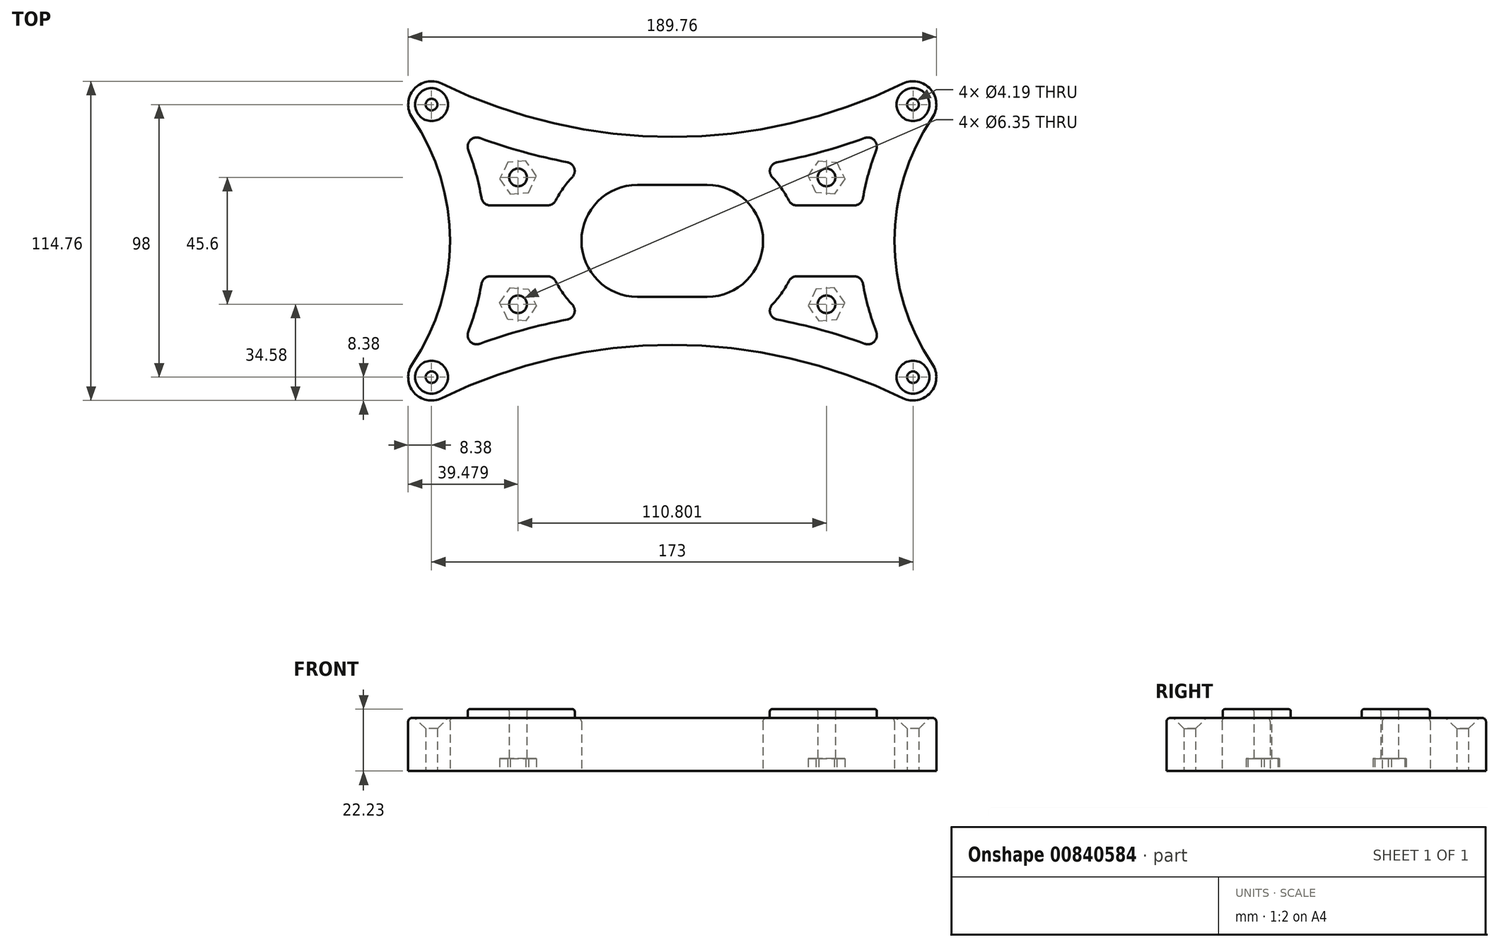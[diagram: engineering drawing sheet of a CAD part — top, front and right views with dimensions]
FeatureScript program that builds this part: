
annotation { "Feature Type Name" : "Feature", "Feature Type Description" : "" }
export const myFeature = defineFeature(function(context is Context, id is Id, definition is map)
    precondition{}
    {
        {
            var Q0;
            Q0=qCreatedBy(makeId("Top.planeOp"),FACE);
            var sketch = newSketch(context, id + "F0", { "sketchPlane" : qUnion([Q0])});
            skLineSegment(sketch, "E0.bottom", {"start": v(-102.5, 65) * mm, "end": v(102.5, 65) * mm, "construction": true});
            skLineSegment(sketch, "E0.top", {"start": v(-102.5, -65) * mm, "end": v(102.5, -65) * mm, "construction": true});
            skLineSegment(sketch, "E0.left", {"start": v(-102.5, 65) * mm, "end": v(-102.5, -65) * mm, "construction": true});
            skLineSegment(sketch, "E0.right", {"start": v(102.5, 65) * mm, "end": v(102.5, -65) * mm, "construction": true});
            skPoint(sketch, "E0.middle", {"position": v(0, 0) * mm});
            skArc(sketch, "E1", {"start": v(-79.48, 63.38) * mm, "mid": v(-98.58, 59.5) * mm, "end": v(-99.76, 40.04) * mm, "construction": true});
            skArc(sketch, "E2.MirrorC", {"start": v(79.48, 63.38) * mm, "mid": v(98.58, 59.5) * mm, "end": v(99.76, 40.04) * mm, "construction": true});
            skArc(sketch, "E3.MirrorC", {"start": v(79.48, -63.38) * mm, "mid": v(98.58, -59.5) * mm, "end": v(99.76, -40.04) * mm, "construction": true});
            skArc(sketch, "E4.MirrorC", {"start": v(-79.48, -63.38) * mm, "mid": v(-98.58, -59.5) * mm, "end": v(-99.76, -40.04) * mm, "construction": true});
            skLineSegment(sketch, "E5", {"start": v(0, 0) * mm, "end": v(0, 365.73) * mm, "construction": true});
            skPoint(sketch, "E5.endSnap0", {"position": v(0, 65) * mm});
            skLineSegment(sketch, "E6", {"start": v(0, 0) * mm, "end": v(0, -420.15) * mm, "construction": true});
            skLineSegment(sketch, "E7", {"start": v(0, 0) * mm, "end": v(397.25, 0) * mm, "construction": true});
            skPoint(sketch, "E7.endSnap0", {"position": v(102.5, 0) * mm});
            skLineSegment(sketch, "E8", {"start": v(0, 0) * mm, "end": v(-430.2, 0) * mm, "construction": true});
            skPoint(sketch, "E9", {"position": v(0, 45) * mm});
            skPoint(sketch, "E10", {"position": v(0, -45) * mm});
            skPoint(sketch, "E11", {"position": v(-87.5, 0) * mm});
            skPoint(sketch, "E12", {"position": v(87.5, 0) * mm});
            skArc(sketch, "E13", {"start": v(-79.48, 63.38) * mm, "mid": v(0, 45) * mm, "end": v(79.48, 63.38) * mm, "construction": true});
            skArc(sketch, "E14.MirrorC", {"start": v(-79.48, -63.38) * mm, "mid": v(0, -45) * mm, "end": v(79.48, -63.38) * mm, "construction": true});
            skArc(sketch, "E15", {"start": v(99.76, 40.04) * mm, "mid": v(87.5, 0) * mm, "end": v(99.76, -40.04) * mm, "construction": true});
            skArc(sketch, "E16.MirrorC", {"start": v(-99.76, 40.04) * mm, "mid": v(-87.5, 0) * mm, "end": v(-99.76, -40.04) * mm, "construction": true});
            skArc(sketch, "E17", {"start": v(-12.5, 12.5) * mm, "mid": v(-25, 0) * mm, "end": v(-12.5, -12.5) * mm, "construction": true});
            skArc(sketch, "E18.MirrorC", {"start": v(12.5, 12.5) * mm, "mid": v(25, 0) * mm, "end": v(12.5, -12.5) * mm, "construction": true});
            skLineSegment(sketch, "E19", {"start": v(-12.5, 12.5) * mm, "end": v(12.5, 12.5) * mm, "construction": true});
            skLineSegment(sketch, "E20", {"start": v(-12.5, -12.5) * mm, "end": v(12.5, -12.5) * mm, "construction": true});
            skArc(sketch, "E21.0", {"start": v(73.54, 32.7) * mm, "mid": v(70.75, 24.17) * mm, "end": v(68.8, 15.41) * mm, "construction": true});
            skArc(sketch, "E21.1", {"start": v(-69.07, 37.24) * mm, "mid": v(-53.53, 32.26) * mm, "end": v(-37.64, 28.55) * mm, "construction": true});
            skArc(sketch, "E21.2", {"start": v(-73.54, 32.7) * mm, "mid": v(-70.75, 24.17) * mm, "end": v(-68.8, 15.41) * mm, "construction": true});
            skArc(sketch, "E21.3", {"start": v(-69.07, -37.24) * mm, "mid": v(-53.53, -32.26) * mm, "end": v(-37.64, -28.55) * mm, "construction": true});
            skArc(sketch, "E22.0", {"start": v(-35.78, 22.67) * mm, "mid": v(-39.02, 18.79) * mm, "end": v(-41.61, 14.44) * mm, "construction": true});
            skArc(sketch, "E22.2", {"start": v(35.78, 22.67) * mm, "mid": v(39.02, 18.79) * mm, "end": v(41.61, 14.44) * mm, "construction": true});
            skPoint(sketch, "E23.visualSharp", {"position": v(-76.83, 40.26) * mm});
            skArc(sketch, "E23.filletArc", {"start": v(-69.07, 37.24) * mm, "mid": v(-72.76, 36.4) * mm, "end": v(-73.54, 32.7) * mm, "construction": true});
            skLineSegment(sketch, "E24", {"start": v(-44.75, 12.5) * mm, "end": v(-65.36, 12.5) * mm, "construction": true});
            skLineSegment(sketch, "E25", {"start": v(-44.75, -12.5) * mm, "end": v(-65.36, -12.5) * mm, "construction": true});
            skLineSegment(sketch, "E26", {"start": v(44.75, 12.5) * mm, "end": v(65.36, 12.5) * mm, "construction": true});
            skLineSegment(sketch, "E27", {"start": v(44.75, -12.5) * mm, "end": v(65.36, -12.5) * mm, "construction": true});
            skArc(sketch, "E28.trimOffspring", {"start": v(41.61, -14.44) * mm, "mid": v(39.02, -18.79) * mm, "end": v(35.78, -22.67) * mm, "construction": true});
            skArc(sketch, "E29.trimOffspring", {"start": v(68.8, -15.41) * mm, "mid": v(70.75, -24.17) * mm, "end": v(73.54, -32.7) * mm, "construction": true});
            skArc(sketch, "E30.trimOffspring", {"start": v(37.64, 28.55) * mm, "mid": v(53.53, 32.26) * mm, "end": v(69.07, 37.24) * mm, "construction": true});
            skArc(sketch, "E31.trimOffspring", {"start": v(37.64, -28.55) * mm, "mid": v(53.53, -32.26) * mm, "end": v(69.07, -37.24) * mm, "construction": true});
            skArc(sketch, "E32.trimOffspring", {"start": v(-41.61, -14.44) * mm, "mid": v(-39.02, -18.79) * mm, "end": v(-35.78, -22.67) * mm, "construction": true});
            skArc(sketch, "E33.trimOffspring", {"start": v(-68.8, -15.41) * mm, "mid": v(-70.75, -24.17) * mm, "end": v(-73.54, -32.7) * mm, "construction": true});
            skPoint(sketch, "E34.visualSharp", {"position": v(-30.17, 27.28) * mm});
            skArc(sketch, "E34.filletArc", {"start": v(-35.78, 22.67) * mm, "mid": v(-34.95, 26.17) * mm, "end": v(-37.64, 28.55) * mm, "construction": true});
            skPoint(sketch, "E35.visualSharp", {"position": v(-42.5, 12.5) * mm});
            skArc(sketch, "E35.filletArc", {"start": v(-44.75, 12.5) * mm, "mid": v(-42.9, 13.03) * mm, "end": v(-41.61, 14.44) * mm, "construction": true});
            skPoint(sketch, "E36.visualSharp", {"position": v(-68.36, 12.5) * mm});
            skArc(sketch, "E36.filletArc", {"start": v(-68.8, 15.41) * mm, "mid": v(-67.61, 13.32) * mm, "end": v(-65.36, 12.5) * mm, "construction": true});
            skPoint(sketch, "E37.visualSharp", {"position": v(-68.36, -12.5) * mm});
            skArc(sketch, "E37.filletArc", {"start": v(-65.36, -12.5) * mm, "mid": v(-67.61, -13.32) * mm, "end": v(-68.8, -15.41) * mm, "construction": true});
            skPoint(sketch, "E38.visualSharp", {"position": v(-42.5, -12.5) * mm});
            skArc(sketch, "E38.filletArc", {"start": v(-41.61, -14.44) * mm, "mid": v(-42.9, -13.03) * mm, "end": v(-44.75, -12.5) * mm, "construction": true});
            skPoint(sketch, "E39.visualSharp", {"position": v(-30.17, -27.28) * mm});
            skArc(sketch, "E39.filletArc", {"start": v(-37.64, -28.55) * mm, "mid": v(-34.95, -26.17) * mm, "end": v(-35.78, -22.67) * mm, "construction": true});
            skPoint(sketch, "E40.visualSharp", {"position": v(-76.83, -40.26) * mm});
            skArc(sketch, "E40.filletArc", {"start": v(-73.54, -32.7) * mm, "mid": v(-72.76, -36.4) * mm, "end": v(-69.07, -37.24) * mm, "construction": true});
            skPoint(sketch, "E41.visualSharp", {"position": v(30.17, 27.28) * mm});
            skArc(sketch, "E41.filletArc", {"start": v(37.64, 28.55) * mm, "mid": v(34.95, 26.17) * mm, "end": v(35.78, 22.67) * mm, "construction": true});
            skPoint(sketch, "E42.visualSharp", {"position": v(76.83, 40.26) * mm});
            skArc(sketch, "E42.filletArc", {"start": v(73.54, 32.7) * mm, "mid": v(72.76, 36.4) * mm, "end": v(69.07, 37.24) * mm, "construction": true});
            skPoint(sketch, "E43.visualSharp", {"position": v(68.36, 12.5) * mm});
            skArc(sketch, "E43.filletArc", {"start": v(65.36, 12.5) * mm, "mid": v(67.61, 13.32) * mm, "end": v(68.8, 15.41) * mm, "construction": true});
            skPoint(sketch, "E44.visualSharp", {"position": v(42.5, 12.5) * mm});
            skArc(sketch, "E44.filletArc", {"start": v(41.61, 14.44) * mm, "mid": v(42.9, 13.03) * mm, "end": v(44.75, 12.5) * mm, "construction": true});
            skPoint(sketch, "E45.visualSharp", {"position": v(42.5, -12.5) * mm});
            skArc(sketch, "E45.filletArc", {"start": v(44.75, -12.5) * mm, "mid": v(42.9, -13.03) * mm, "end": v(41.61, -14.44) * mm, "construction": true});
            skPoint(sketch, "E46.visualSharp", {"position": v(68.36, -12.5) * mm});
            skArc(sketch, "E46.filletArc", {"start": v(68.8, -15.41) * mm, "mid": v(67.61, -13.32) * mm, "end": v(65.36, -12.5) * mm, "construction": true});
            skPoint(sketch, "E47.visualSharp", {"position": v(76.83, -40.26) * mm});
            skArc(sketch, "E47.filletArc", {"start": v(69.07, -37.24) * mm, "mid": v(72.76, -36.4) * mm, "end": v(73.54, -32.7) * mm, "construction": true});
            skPoint(sketch, "E48.visualSharp", {"position": v(30.17, -27.28) * mm});
            skArc(sketch, "E48.filletArc", {"start": v(35.78, -22.67) * mm, "mid": v(34.95, -26.17) * mm, "end": v(37.64, -28.55) * mm, "construction": true});
            skArc(sketch, "E49.0", {"start": v(-82.82, 56.53) * mm, "mid": v(-92.82, 54.5) * mm, "end": v(-93.44, 44.3) * mm});
            skArc(sketch, "E49.1", {"start": v(-93.44, 44.3) * mm, "mid": v(-79.88, 0) * mm, "end": v(-93.44, -44.3) * mm});
            skArc(sketch, "E49.2", {"start": v(-82.82, 56.53) * mm, "mid": v(0, 37.38) * mm, "end": v(82.82, 56.53) * mm});
            skArc(sketch, "E49.3", {"start": v(-82.82, -56.53) * mm, "mid": v(-92.82, -54.5) * mm, "end": v(-93.44, -44.3) * mm});
            skArc(sketch, "E49.4", {"start": v(82.82, 56.53) * mm, "mid": v(92.82, 54.5) * mm, "end": v(93.44, 44.3) * mm});
            skArc(sketch, "E49.5", {"start": v(93.44, 44.3) * mm, "mid": v(79.88, 0) * mm, "end": v(93.44, -44.3) * mm});
            skArc(sketch, "E49.6", {"start": v(82.82, -56.53) * mm, "mid": v(92.82, -54.5) * mm, "end": v(93.44, -44.3) * mm});
            skArc(sketch, "E49.7", {"start": v(-82.82, -56.53) * mm, "mid": v(0, -37.38) * mm, "end": v(82.82, -56.53) * mm});
            skCircle(sketch, "E50", {"center": v(-86.5, -49) * mm, "radius": 2.1 * mm});
            skCircle(sketch, "E51", {"center": v(86.5, -49) * mm, "radius": 2.1 * mm});
            skCircle(sketch, "E52", {"center": v(86.5, 49) * mm, "radius": 2.1 * mm});
            skCircle(sketch, "E53", {"center": v(-86.5, 49) * mm, "radius": 2.1 * mm});
            skArc(sketch, "E54.0", {"start": v(-41.84, -14.56) * mm, "mid": v(-43.04, -13.24) * mm, "end": v(-44.75, -12.75) * mm});
            skArc(sketch, "E54.1", {"start": v(-41.84, -14.56) * mm, "mid": v(-39.23, -18.93) * mm, "end": v(-35.97, -22.85) * mm});
            skLineSegment(sketch, "E54.2", {"start": v(-44.75, -12.75) * mm, "end": v(-65.36, -12.75) * mm});
            skArc(sketch, "E54.3", {"start": v(-37.68, -28.3) * mm, "mid": v(-35.2, -26.1) * mm, "end": v(-35.97, -22.85) * mm});
            skArc(sketch, "E54.4", {"start": v(-65.36, -12.75) * mm, "mid": v(-67.45, -13.52) * mm, "end": v(-68.56, -15.45) * mm});
            skArc(sketch, "E54.5", {"start": v(-68.56, -15.45) * mm, "mid": v(-70.5, -24.24) * mm, "end": v(-73.3, -32.79) * mm});
            skArc(sketch, "E54.6", {"start": v(-73.3, -32.79) * mm, "mid": v(-72.58, -36.23) * mm, "end": v(-69.16, -37) * mm});
            skArc(sketch, "E54.7", {"start": v(-69.16, -37) * mm, "mid": v(-53.6, -32.01) * mm, "end": v(-37.68, -28.3) * mm});
            skArc(sketch, "E55.0", {"start": v(68.56, -15.45) * mm, "mid": v(67.45, -13.52) * mm, "end": v(65.36, -12.75) * mm});
            skLineSegment(sketch, "E55.1", {"start": v(44.75, -12.75) * mm, "end": v(65.36, -12.75) * mm});
            skArc(sketch, "E55.2", {"start": v(68.56, -15.45) * mm, "mid": v(70.5, -24.24) * mm, "end": v(73.3, -32.79) * mm});
            skArc(sketch, "E55.3", {"start": v(44.75, -12.75) * mm, "mid": v(43.04, -13.24) * mm, "end": v(41.84, -14.56) * mm});
            skArc(sketch, "E55.4", {"start": v(69.16, -37) * mm, "mid": v(72.58, -36.23) * mm, "end": v(73.3, -32.79) * mm});
            skArc(sketch, "E55.5", {"start": v(37.68, -28.3) * mm, "mid": v(53.6, -32.01) * mm, "end": v(69.16, -37) * mm});
            skArc(sketch, "E55.6", {"start": v(35.97, -22.85) * mm, "mid": v(35.2, -26.1) * mm, "end": v(37.68, -28.3) * mm});
            skArc(sketch, "E55.7", {"start": v(41.84, -14.56) * mm, "mid": v(39.23, -18.93) * mm, "end": v(35.97, -22.85) * mm});
            skArc(sketch, "E56.0", {"start": v(37.68, 28.3) * mm, "mid": v(35.2, 26.1) * mm, "end": v(35.97, 22.85) * mm});
            skArc(sketch, "E56.1", {"start": v(35.97, 22.85) * mm, "mid": v(39.23, 18.93) * mm, "end": v(41.84, 14.56) * mm});
            skArc(sketch, "E56.2", {"start": v(37.68, 28.3) * mm, "mid": v(53.6, 32.01) * mm, "end": v(69.16, 37) * mm});
            skArc(sketch, "E56.3", {"start": v(41.84, 14.56) * mm, "mid": v(43.04, 13.24) * mm, "end": v(44.75, 12.75) * mm});
            skArc(sketch, "E56.4", {"start": v(73.3, 32.79) * mm, "mid": v(72.58, 36.23) * mm, "end": v(69.16, 37) * mm});
            skArc(sketch, "E56.5", {"start": v(73.3, 32.79) * mm, "mid": v(70.5, 24.24) * mm, "end": v(68.56, 15.45) * mm});
            skArc(sketch, "E56.6", {"start": v(65.36, 12.75) * mm, "mid": v(67.45, 13.52) * mm, "end": v(68.56, 15.45) * mm});
            skLineSegment(sketch, "E56.7", {"start": v(44.75, 12.75) * mm, "end": v(65.36, 12.75) * mm});
            skArc(sketch, "E57.0", {"start": v(-69.16, 37) * mm, "mid": v(-72.58, 36.23) * mm, "end": v(-73.3, 32.79) * mm});
            skArc(sketch, "E57.1", {"start": v(-73.3, 32.79) * mm, "mid": v(-70.5, 24.24) * mm, "end": v(-68.56, 15.45) * mm});
            skArc(sketch, "E57.2", {"start": v(-69.16, 37) * mm, "mid": v(-53.6, 32.01) * mm, "end": v(-37.68, 28.3) * mm});
            skArc(sketch, "E57.3", {"start": v(-68.56, 15.45) * mm, "mid": v(-67.45, 13.52) * mm, "end": v(-65.36, 12.75) * mm});
            skArc(sketch, "E57.4", {"start": v(-35.97, 22.85) * mm, "mid": v(-35.2, 26.1) * mm, "end": v(-37.68, 28.3) * mm});
            skArc(sketch, "E57.5", {"start": v(-35.97, 22.85) * mm, "mid": v(-39.23, 18.93) * mm, "end": v(-41.84, 14.56) * mm});
            skArc(sketch, "E57.6", {"start": v(-44.75, 12.75) * mm, "mid": v(-43.04, 13.24) * mm, "end": v(-41.84, 14.56) * mm});
            skLineSegment(sketch, "E57.7", {"start": v(-44.75, 12.75) * mm, "end": v(-65.36, 12.75) * mm});
            skLineSegment(sketch, "E58.0", {"start": v(-12.5, 20.12) * mm, "end": v(12.5, 20.12) * mm});
            skArc(sketch, "E58.1", {"start": v(-12.5, 20.12) * mm, "mid": v(-32.62, 0) * mm, "end": v(-12.5, -20.12) * mm});
            skLineSegment(sketch, "E58.2", {"start": v(-12.5, -20.12) * mm, "end": v(12.5, -20.12) * mm});
            skArc(sketch, "E58.3", {"start": v(12.5, 20.12) * mm, "mid": v(32.62, 0) * mm, "end": v(12.5, -20.12) * mm});
            skPoint(sketch, "E59", {"position": v(-55.4, 22.8) * mm});
            skPoint(sketch, "E60.MirrorP", {"position": v(-55.4, -22.8) * mm});
            skPoint(sketch, "E61.MirrorP", {"position": v(55.4, -22.8) * mm});
            skPoint(sketch, "E62.MirrorP", {"position": v(55.4, 22.8) * mm});
            skCircle(sketch, "E63", {"center": v(-55.4, -22.8) * mm, "radius": 3.18 * mm});
            skCircle(sketch, "E64.cCircle", {"center": v(-55.4, -22.8) * mm, "radius": 5.72 * mm, "construction": true});
            skLineSegment(sketch, "E64.0", {"start": v(-61.98, -22.26) * mm, "end": v(-58.22, -16.83) * mm});
            skLineSegment(sketch, "E64.1", {"start": v(-58.22, -16.83) * mm, "end": v(-51.64, -17.37) * mm});
            skLineSegment(sketch, "E64.2", {"start": v(-51.64, -17.37) * mm, "end": v(-48.82, -23.34) * mm});
            skLineSegment(sketch, "E64.3", {"start": v(-48.82, -23.34) * mm, "end": v(-52.58, -28.77) * mm});
            skLineSegment(sketch, "E64.4", {"start": v(-52.58, -28.77) * mm, "end": v(-59.16, -28.23) * mm});
            skLineSegment(sketch, "E64.5", {"start": v(-59.16, -28.23) * mm, "end": v(-61.98, -22.26) * mm});
            skPoint(sketch, "E64.0.midPoint", {"position": v(-60.1, -19.55) * mm});
            skLineSegment(sketch, "E65.MirrorCS", {"start": v(-51.64, 17.37) * mm, "end": v(-48.82, 23.34) * mm});
            skLineSegment(sketch, "E66.MirrorCS", {"start": v(-61.98, 22.26) * mm, "end": v(-58.22, 16.83) * mm});
            skLineSegment(sketch, "E67.MirrorCS", {"start": v(-52.58, 28.77) * mm, "end": v(-59.16, 28.23) * mm});
            skLineSegment(sketch, "E68.MirrorCS", {"start": v(-59.16, 28.23) * mm, "end": v(-61.98, 22.26) * mm});
            skCircle(sketch, "E69.MirrorC", {"center": v(-55.4, 22.8) * mm, "radius": 3.18 * mm});
            skPoint(sketch, "E70.MirrorP", {"position": v(-60.1, 19.55) * mm});
            skLineSegment(sketch, "E71.MirrorCS", {"start": v(-48.82, 23.34) * mm, "end": v(-52.58, 28.77) * mm});
            skLineSegment(sketch, "E72.MirrorCS", {"start": v(-58.22, 16.83) * mm, "end": v(-51.64, 17.37) * mm});
            skCircle(sketch, "E73.MirrorC", {"center": v(-55.4, 22.8) * mm, "radius": 5.72 * mm, "construction": true});
            skLineSegment(sketch, "E74.MirrorCS", {"start": v(58.22, 16.83) * mm, "end": v(51.64, 17.37) * mm});
            skLineSegment(sketch, "E75.MirrorCS", {"start": v(48.82, 23.34) * mm, "end": v(52.58, 28.77) * mm});
            skPoint(sketch, "E76.MirrorP", {"position": v(60.1, 19.55) * mm});
            skLineSegment(sketch, "E77.MirrorCS", {"start": v(52.58, 28.77) * mm, "end": v(59.16, 28.23) * mm});
            skLineSegment(sketch, "E78.MirrorCS", {"start": v(59.16, 28.23) * mm, "end": v(61.98, 22.26) * mm});
            skCircle(sketch, "E79.MirrorC", {"center": v(55.4, 22.8) * mm, "radius": 5.72 * mm, "construction": true});
            skLineSegment(sketch, "E80.MirrorCS", {"start": v(61.98, 22.26) * mm, "end": v(58.22, 16.83) * mm});
            skLineSegment(sketch, "E81.MirrorCS", {"start": v(51.64, 17.37) * mm, "end": v(48.82, 23.34) * mm});
            skCircle(sketch, "E82.MirrorC", {"center": v(55.4, 22.8) * mm, "radius": 3.18 * mm});
            skLineSegment(sketch, "E83.MirrorCS", {"start": v(48.82, -23.34) * mm, "end": v(52.58, -28.77) * mm});
            skLineSegment(sketch, "E84.MirrorCS", {"start": v(51.64, -17.37) * mm, "end": v(48.82, -23.34) * mm});
            skPoint(sketch, "E85.MirrorP", {"position": v(60.1, -19.55) * mm});
            skLineSegment(sketch, "E86.MirrorCS", {"start": v(59.16, -28.23) * mm, "end": v(61.98, -22.26) * mm});
            skCircle(sketch, "E87.MirrorC", {"center": v(55.4, -22.8) * mm, "radius": 5.72 * mm, "construction": true});
            skLineSegment(sketch, "E88.MirrorCS", {"start": v(61.98, -22.26) * mm, "end": v(58.22, -16.83) * mm});
            skLineSegment(sketch, "E89.MirrorCS", {"start": v(52.58, -28.77) * mm, "end": v(59.16, -28.23) * mm});
            skLineSegment(sketch, "E90.MirrorCS", {"start": v(58.22, -16.83) * mm, "end": v(51.64, -17.37) * mm});
            skCircle(sketch, "E91.MirrorC", {"center": v(55.4, -22.8) * mm, "radius": 3.18 * mm});
            skSolve(sketch);
        }
        {
            var Q0;
            Q0=makeQuery(id+"F0.imprint","IMPRINT",FACE,{"disambiguationData":[TD([[makeQuery(id+"F0.imprint","IMPRINT",EDGE,{"derivedFrom":sQuery(id+"F0.wireOp",EDGE,"E49.0")}),1.0]])]});
            extrude(context, id + "F1", {"entities" : qUnion([Q0]), "depth" : 19.05 * mm, "offsetDistance" : 25.4 * mm});
        }
        {
            var Q0;
            Q0=makeQuery(id+"F0.imprint","IMPRINT",FACE,{"disambiguationData":[TD([[makeQuery(id+"F0.imprint","IMPRINT",EDGE,{"derivedFrom":sQuery(id+"F0.wireOp",EDGE,"E57.0")}),1.0]])]});
            var Q1;
            Q1=makeQuery(id+"F0.imprint","IMPRINT",FACE,{"disambiguationData":[TD([[makeQuery(id+"F0.imprint","IMPRINT",EDGE,{"derivedFrom":sQuery(id+"F0.wireOp",EDGE,"E54.0")}),1.0]])]});
            var Q2;
            Q2=makeQuery(id+"F0.imprint","IMPRINT",FACE,{"disambiguationData":[TD([[makeQuery(id+"F0.imprint","IMPRINT",EDGE,{"derivedFrom":sQuery(id+"F0.wireOp",EDGE,"E55.0")}),1.0]])]});
            var Q3;
            Q3=makeQuery(id+"F0.imprint","IMPRINT",FACE,{"disambiguationData":[TD([[makeQuery(id+"F0.imprint","IMPRINT",EDGE,{"derivedFrom":sQuery(id+"F0.wireOp",EDGE,"E56.0")}),1.0]])]});
            var Q4;
            Q4=makeQuery(id+"F0.imprint","IMPRINT",FACE,{"disambiguationData":[TD([[makeQuery(id+"F0.imprint","IMPRINT",EDGE,{"derivedFrom":sQuery(id+"F0.wireOp",EDGE,"E74.MirrorCS")}),-1.0]])]});
            var Q5;
            Q5=makeQuery(id+"F0.imprint","IMPRINT",FACE,{"disambiguationData":[TD([[makeQuery(id+"F0.imprint","IMPRINT",EDGE,{"derivedFrom":sQuery(id+"F0.wireOp",EDGE,"E83.MirrorCS")}),1.0]])]});
            var Q6;
            Q6=makeQuery(id+"F0.imprint","IMPRINT",FACE,{"disambiguationData":[TD([[makeQuery(id+"F0.imprint","IMPRINT",EDGE,{"derivedFrom":sQuery(id+"F0.wireOp",EDGE,"E63")}),-1.0]])]});
            var Q7;
            Q7=makeQuery(id+"F0.imprint","IMPRINT",FACE,{"disambiguationData":[TD([[makeQuery(id+"F0.imprint","IMPRINT",EDGE,{"derivedFrom":sQuery(id+"F0.wireOp",EDGE,"E65.MirrorCS")}),1.0]])]});
            extrude(context, id + "F2", {"entities" : qUnion([Q0, Q1, Q2, Q3, Q4, Q5, Q6, Q7]), "operationType" : NewBodyOperationType.ADD, "depth" : 22.22 * mm, "offsetDistance" : 25.4 * mm});
        }
        {
            var Q0;
            Q0=makeQuery(id+"F0.imprint","IMPRINT",FACE,{"disambiguationData":[TD([[makeQuery(id+"F0.imprint","IMPRINT",EDGE,{"derivedFrom":sQuery(id+"F0.wireOp",EDGE,"E65.MirrorCS")}),1.0]])]});
            var Q1;
            Q1=makeQuery(id+"F0.imprint","IMPRINT",FACE,{"disambiguationData":[TD([[makeQuery(id+"F0.imprint","IMPRINT",EDGE,{"derivedFrom":sQuery(id+"F0.wireOp",EDGE,"E74.MirrorCS")}),-1.0]])]});
            var Q2;
            Q2=makeQuery(id+"F0.imprint","IMPRINT",FACE,{"disambiguationData":[TD([[makeQuery(id+"F0.imprint","IMPRINT",EDGE,{"derivedFrom":sQuery(id+"F0.wireOp",EDGE,"E83.MirrorCS")}),1.0]])]});
            var Q3;
            Q3=makeQuery(id+"F0.imprint","IMPRINT",FACE,{"disambiguationData":[TD([[makeQuery(id+"F0.imprint","IMPRINT",EDGE,{"derivedFrom":sQuery(id+"F0.wireOp",EDGE,"E63")}),-1.0]])]});
            extrude(context, id + "F3", {"entities" : qUnion([Q0, Q1, Q2, Q3]), "operationType" : NewBodyOperationType.REMOVE, "depth" : 4.44 * mm, "offsetDistance" : 25.4 * mm});
        }
        {
            var Q0;
            Q0=makeQuery(id+"F1.opExtrude","CAP_EDGE",EDGE,{"disambiguationData":[OSD([sQuery(id+"F0.wireOp",EDGE,"E52")])],"isStart":false});
            var Q1;
            Q1=makeQuery(id+"F1.opExtrude","CAP_EDGE",EDGE,{"disambiguationData":[OSD([sQuery(id+"F0.wireOp",EDGE,"E51")])],"isStart":false});
            var Q2;
            Q2=makeQuery(id+"F1.opExtrude","CAP_EDGE",EDGE,{"disambiguationData":[OSD([sQuery(id+"F0.wireOp",EDGE,"E50")])],"isStart":false});
            var Q3;
            Q3=makeQuery(id+"F1.opExtrude","CAP_EDGE",EDGE,{"disambiguationData":[OSD([sQuery(id+"F0.wireOp",EDGE,"E53")])],"isStart":false});
            chamfer(context, id + "F4", {"entities" : qUnion([Q0, Q1, Q2, Q3]), "width" : 3.8 * mm, "tangentPropagation" : true});
        }
        {
            var Q0;
            Q0=makeQuery(id+"F1.opExtrude","CAP_EDGE",EDGE,{"disambiguationData":[OSD([sQuery(id+"F0.wireOp",EDGE,"E49.1")])],"isStart":false});
            var Q1;
            Q1=makeQuery(id+"F1.opExtrude","CAP_EDGE",EDGE,{"disambiguationData":[OSD([sQuery(id+"F0.wireOp",EDGE,"E49.3")])],"isStart":false});
            var Q2;
            Q2=makeQuery(id+"F1.opExtrude","CAP_EDGE",EDGE,{"disambiguationData":[OSD([sQuery(id+"F0.wireOp",EDGE,"E49.7")])],"isStart":false});
            var Q3;
            Q3=makeQuery(id+"F1.opExtrude","CAP_EDGE",EDGE,{"disambiguationData":[OSD([sQuery(id+"F0.wireOp",EDGE,"E49.6")])],"isStart":false});
            var Q4;
            Q4=makeQuery(id+"F1.opExtrude","CAP_EDGE",EDGE,{"disambiguationData":[OSD([sQuery(id+"F0.wireOp",EDGE,"E49.5")])],"isStart":false});
            var Q5;
            Q5=makeQuery(id+"F1.opExtrude","CAP_EDGE",EDGE,{"disambiguationData":[OSD([sQuery(id+"F0.wireOp",EDGE,"E49.4")])],"isStart":false});
            var Q6;
            Q6=makeQuery(id+"F1.opExtrude","CAP_EDGE",EDGE,{"disambiguationData":[OSD([sQuery(id+"F0.wireOp",EDGE,"E49.2")])],"isStart":false});
            var Q7;
            Q7=makeQuery(id+"F1.opExtrude","CAP_EDGE",EDGE,{"disambiguationData":[OSD([sQuery(id+"F0.wireOp",EDGE,"E49.0")])],"isStart":false});
            var Q8;
            Q8=makeQuery(id+"F1.opExtrude","CAP_EDGE",EDGE,{"disambiguationData":[OSD([sQuery(id+"F0.wireOp",EDGE,"E58.1")])],"isStart":false});
            var Q9;
            Q9=makeQuery(id+"F1.opExtrude","CAP_EDGE",EDGE,{"disambiguationData":[OSD([sQuery(id+"F0.wireOp",EDGE,"E58.0")])],"isStart":false});
            fillet(context, id + "F5", {"entities" : qUnion([Q0, Q1, Q2, Q3, Q4, Q5, Q6, Q7, Q8, Q9]), "radius" : 1.27 * mm, "tangentPropagation" : true, "allowEdgeOverflow" : false});
        }
        {
            var Q0;
            Q0=makeQuery(id+"F2.opExtrude","CAP_EDGE",EDGE,{"disambiguationData":[OSD([sQuery(id+"F0.wireOp",EDGE,"E57.7")])],"isStart":false});
            var Q1;
            Q1=makeQuery(id+"F2.opExtrude","CAP_EDGE",EDGE,{"disambiguationData":[OSD([sQuery(id+"F0.wireOp",EDGE,"E56.7")])],"isStart":false});
            var Q2;
            Q2=makeQuery(id+"F2.opExtrude","CAP_EDGE",EDGE,{"disambiguationData":[OSD([sQuery(id+"F0.wireOp",EDGE,"E55.5")])],"isStart":false});
            var Q3;
            Q3=makeQuery(id+"F2.opExtrude","CAP_EDGE",EDGE,{"disambiguationData":[OSD([sQuery(id+"F0.wireOp",EDGE,"E54.7")])],"isStart":false});
            var Q4;
            Q4=makeQuery(id+"F2.opExtrude","CAP_EDGE",EDGE,{"disambiguationData":[OSD([sQuery(id+"F0.wireOp",EDGE,"E91.MirrorC")])],"isStart":false});
            var Q5;
            Q5=makeQuery(id+"F2.opExtrude","CAP_EDGE",EDGE,{"disambiguationData":[OSD([sQuery(id+"F0.wireOp",EDGE,"E82.MirrorC")])],"isStart":false});
            var Q6;
            Q6=makeQuery(id+"F2.opExtrude","CAP_EDGE",EDGE,{"disambiguationData":[OSD([sQuery(id+"F0.wireOp",EDGE,"E63")])],"isStart":false});
            var Q7;
            Q7=makeQuery(id+"F2.opExtrude","CAP_EDGE",EDGE,{"disambiguationData":[OSD([sQuery(id+"F0.wireOp",EDGE,"E69.MirrorC")])],"isStart":false});
            fillet(context, id + "F6", {"entities" : qUnion([Q0, Q1, Q2, Q3, Q4, Q5, Q6, Q7]), "radius" : 0.76 * mm, "tangentPropagation" : true, "allowEdgeOverflow" : false});
        }
    });
